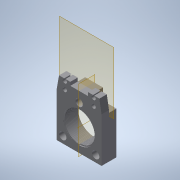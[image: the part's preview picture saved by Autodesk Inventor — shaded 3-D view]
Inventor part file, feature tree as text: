
AUTODESK INVENTOR PART (.ipt)
format: ipt  version: 2022 (Build 260153000, 153)  size: 649,216 bytes
history: native  units: mm
features: other x7, extrude x6, sketch x6, reference x6, projected_geometry x3, plane x2, helix x1
ambient origin geometry x8: Origin, YZ Plane, XZ Plane, XY Plane, X Axis, Y Axis, Z Axis, Center Point
bodies: Solid1 (feature_tree)
feature tree (31):
  plane  "Work Plane1"
  extrude  "Extrusion1"  Depth=30.0mm
  extrude  "Extrusion2"  Depth=5.0mm TaperAngle=0.0deg
  extrude  "Extrusion4"  Depth=5.0mm TaperAngle=0.0deg
  extrude  "Extrusion5"  Depth=1.0mm TaperAngle=0.0deg
  extrude  "Extrusion6"  Depth=9.95mm
  plane  "Work Plane2"
  other  "Work Axis2"
  helix  "Coil1"  [1 undecoded]
  extrude  "Extrusion10"  Depth=10.0mm
  sketch  "Sketch1"  dims[d0=25.0mm d1=30.0mm]
  reference  "Reference1"
  reference  "Reference2"
  sketch  "Sketch2"  dims[d2=30.0mm d3=5.0mm d4=0.0mm]
  reference  "Reference3"
  reference  "Reference4"
  reference  "Reference5"
  projected_geometry  "Projected Loop1"
  sketch  "Sketch4"  dims[d5=21.0mm d6=5.0mm d7=0.0mm]
  sketch  "Sketch5"  dims[d10=5.0mm d11=0.0mm d12=1.0mm d13=0.0mm]
  projected_geometry  "Projected Loop2"
  sketch  "Sketch6"  dims[d14=1.0mm d15=0.0mm]
  reference  "Reference7"
  sketch  "Sketch10"  dims[d16=0.15mm d17=0.0mm d18=120.0deg d19=0.15mm d20=120.0deg d21=1.0mm d22=0.713333mm d25=0.713333mm d26=10.0mm d27=130.0mm d28=0.0mm d29=90.0deg d30=90.0deg d31=0.0mm d32=0.0mm d33=9.95mm d43=4.9mm d44=4.9mm d45=4.9mm d46=10.0mm d47=0.0mm]
  projected_geometry  "Projected Loop4"
  other  "Assembly_Cube_Z_Focus_MGN_NEMA_v3.iam"
  other  "30_Cube_Z_Focus_MGN_NEMA_slide:1"
  other  "00_Microscope_Objective_Lens10x:1"
  other  "Assembly_Cube_empty_IM_v3:2"
  other  "10_Cube_1x1_IM:1"
  other  "00_RMS_Thread:1"
note: 1 required parameter value undecoded (feature->parameter linkage not recoverable at this tier; creation-order binding heuristic only, values carry confidence <= 0.55)
